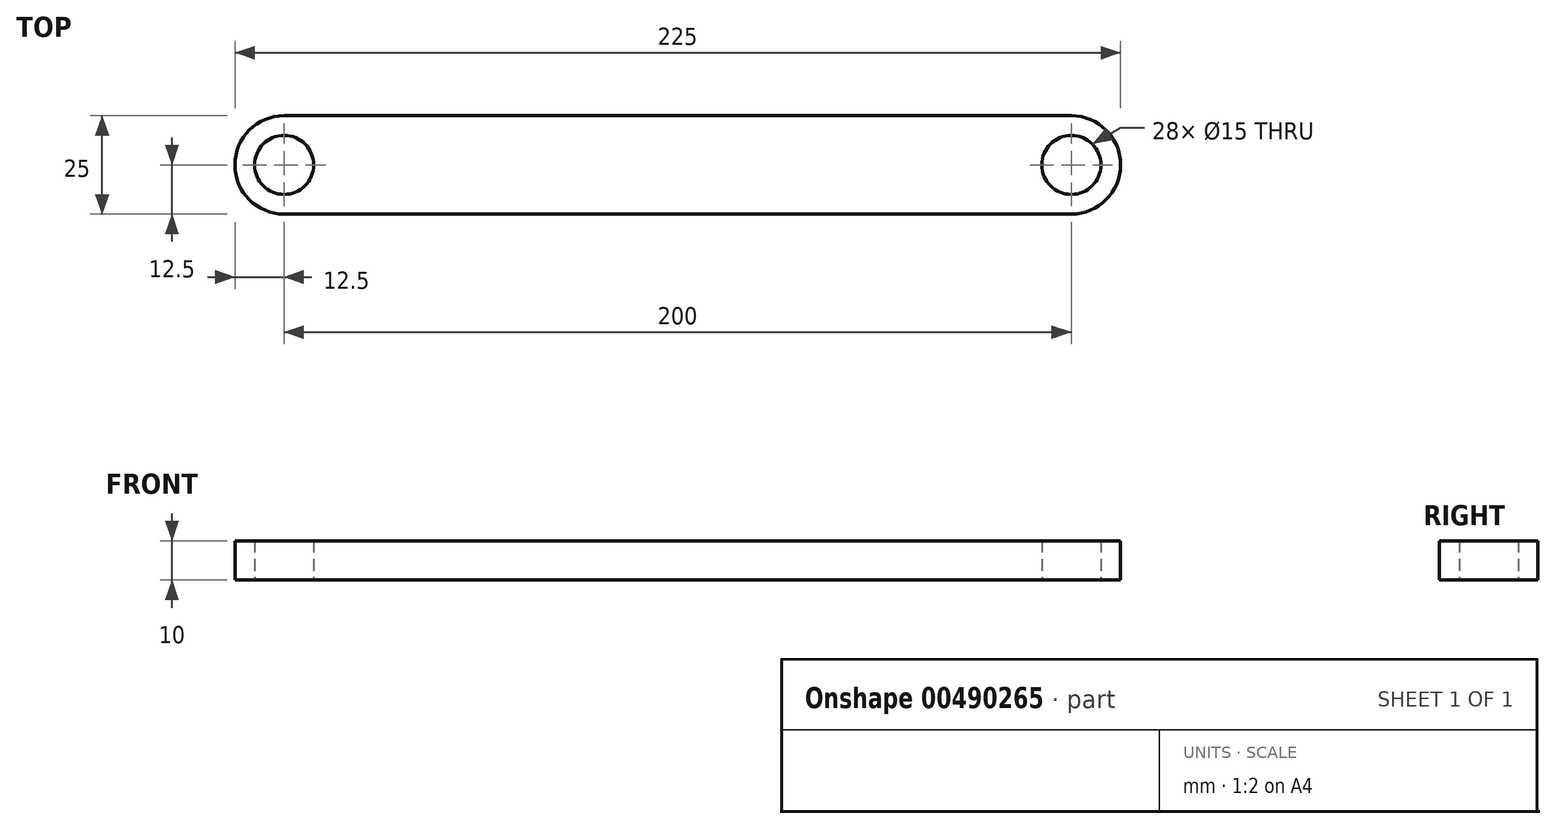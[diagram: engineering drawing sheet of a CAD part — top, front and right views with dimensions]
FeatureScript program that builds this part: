
annotation { "Feature Type Name" : "Feature", "Feature Type Description" : "" }
export const myFeature = defineFeature(function(context is Context, id is Id, definition is map)
    precondition{}
    {
        {
            var Q0;
            Q0=qCreatedBy(makeId("Top.planeOp"),FACE);
            var sketch = newSketch(context, id + "F0", { "sketchPlane" : qUnion([Q0])});
            skLineSegment(sketch, "E0.bottom", {"start": v(0, 0) * mm, "end": v(-200, 0) * mm});
            skLineSegment(sketch, "E0.top", {"start": v(0, 25) * mm, "end": v(-200, 25) * mm});
            skArc(sketch, "E1", {"start": v(-200, 25) * mm, "mid": v(-212.5, 12.5) * mm, "end": v(-200, 0) * mm});
            skArc(sketch, "E2", {"start": v(0, 0) * mm, "mid": v(12.5, 12.5) * mm, "end": v(0, 25) * mm});
            skCircle(sketch, "E3", {"center": v(-200, 12.5) * mm, "radius": 7.5 * mm});
            skCircle(sketch, "E4", {"center": v(0, 12.5) * mm, "radius": 7.5 * mm});
            skSolve(sketch);
        }
        {
            var Q0;
            Q0 = qSketchRegion(id + "F0", true);
            extrude(context, id + "F1", {"entities" : qUnion([Q0]), "depth" : 10 * mm});
        }
    });
